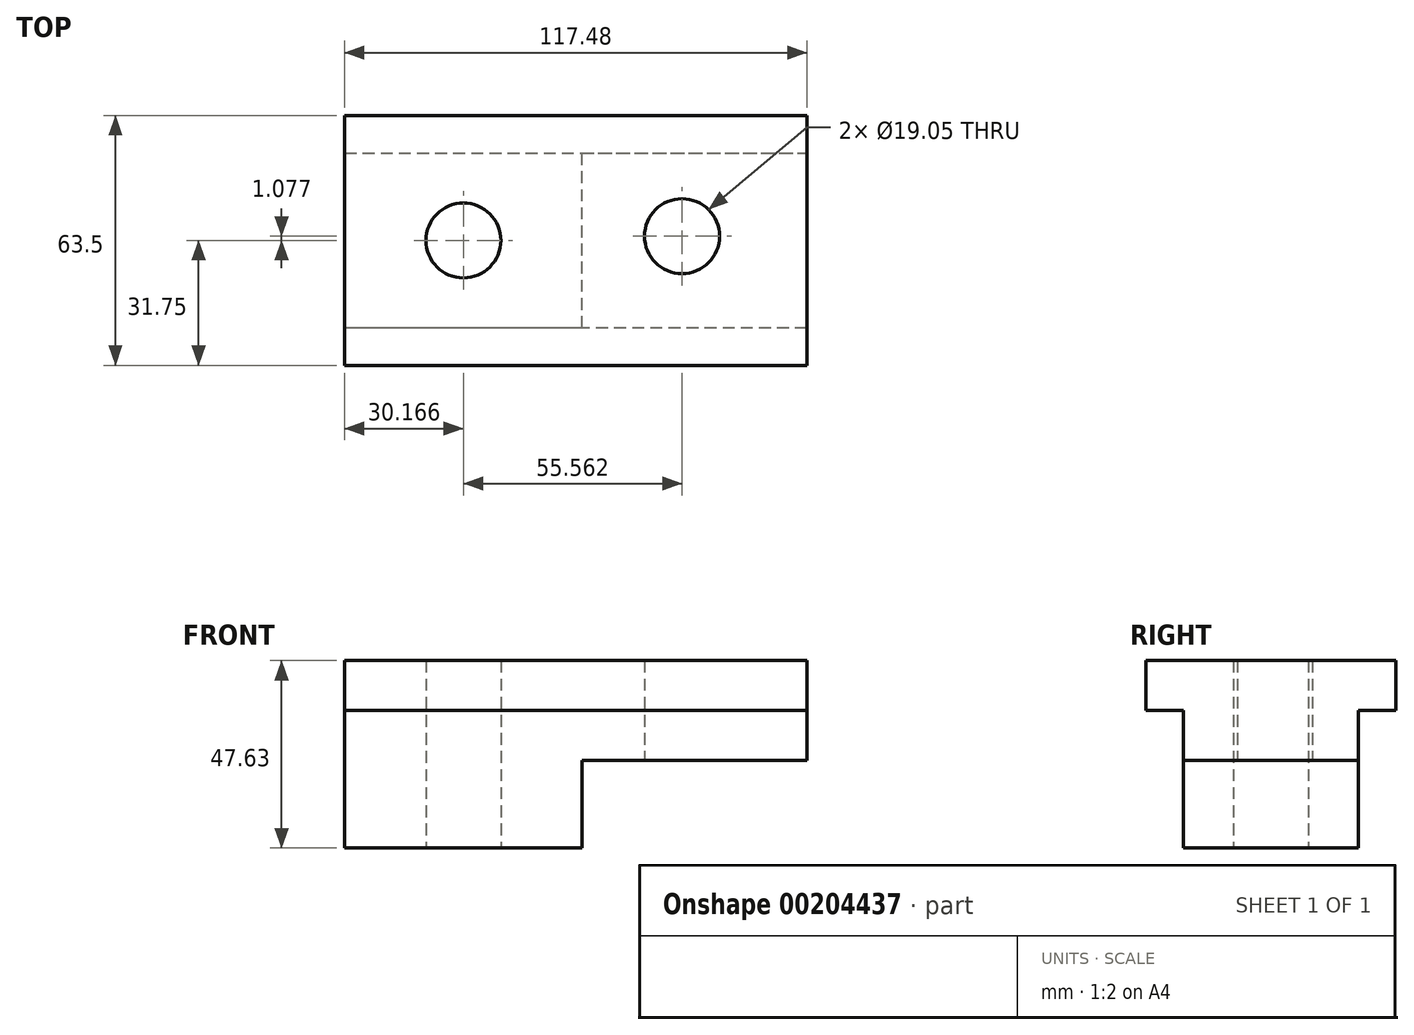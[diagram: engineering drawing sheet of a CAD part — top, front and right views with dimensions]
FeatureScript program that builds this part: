
annotation { "Feature Type Name" : "Feature", "Feature Type Description" : "" }
export const myFeature = defineFeature(function(context is Context, id is Id, definition is map)
    precondition{}
    {
        {
            var Q0;
            Q0=qCreatedBy(makeId("Top.planeOp"),FACE);
            var sketch = newSketch(context, id + "F0", { "sketchPlane" : qUnion([Q0])});
            skLineSegment(sketch, "E0.bottom", {"start": v(-57.42, 26.1) * mm, "end": v(60.06, 26.1) * mm});
            skLineSegment(sketch, "E0.top", {"start": v(-57.42, -37.4) * mm, "end": v(60.06, -37.4) * mm});
            skLineSegment(sketch, "E0.left", {"start": v(-57.42, 26.1) * mm, "end": v(-57.42, -37.4) * mm});
            skLineSegment(sketch, "E0.right", {"start": v(60.06, 26.1) * mm, "end": v(60.06, -37.4) * mm});
            skSolve(sketch);
        }
        {
            var Q0;
            Q0=makeQuery(id+"F0.imprint","IMPRINT",FACE,{"disambiguationData":[TD([[makeQuery(id+"F0.imprint","IMPRINT",EDGE,{"derivedFrom":sQuery(id+"F0.wireOp",EDGE,"E0.bottom")}),-1.0]])]});
            extrude(context, id + "F1", {"entities" : qUnion([Q0]), "depth" : 12.7 * mm});
        }
        {
            var Q0;
            Q0=makeQuery(id+"F1.opExtrude","CAP_FACE",FACE,{"disambiguationData":[OSD([sQuery(id+"F0.wireOp",EDGE,"E0.bottom"),sQuery(id+"F0.wireOp",EDGE,"E0.top"),sQuery(id+"F0.wireOp",EDGE,"E0.left"),sQuery(id+"F0.wireOp",EDGE,"E0.right")])],"isStart":true});
            var sketch = newSketch(context, id + "F2", { "sketchPlane" : qUnion([Q0])});
            skLineSegment(sketch, "E1", {"start": v(-57.42, -26.1) * mm, "end": v(-57.42, -16.57) * mm});
            skLineSegment(sketch, "E2", {"start": v(-57.42, 37.4) * mm, "end": v(-57.42, 27.88) * mm});
            skLineSegment(sketch, "E3", {"start": v(-57.42, -16.57) * mm, "end": v(60.06, -16.57) * mm});
            skLineSegment(sketch, "E4", {"start": v(60.06, -16.57) * mm, "end": v(60.06, 27.88) * mm});
            skLineSegment(sketch, "E5", {"start": v(60.06, 27.88) * mm, "end": v(-57.42, 27.88) * mm});
            skSolve(sketch);
        }
        {
            var Q0;
            {var subQ0=sQuery(id+"F2.wireOp",EDGE,"E3");Q0=makeQuery(id+"F2.imprint","IMPRINT",FACE,{"disambiguationData":[TD([[makeQuery(id+"F2.imprint","IMPRINT",EDGE,{"derivedFrom":subQ0}),1.0]])]});}
            extrude(context, id + "F3", {"entities" : qUnion([Q0]), "operationType" : NewBodyOperationType.ADD, "depth" : 12.7 * mm});
        }
        {
            var Q0;
            Q0=makeQuery(id+"F3.opExtrude","CAP_FACE",FACE,{"disambiguationData":[OSD([sQuery(id+"F0.wireOp",EDGE,"E0.left"),sQuery(id+"F2.wireOp",EDGE,"E3"),sQuery(id+"F2.wireOp",EDGE,"E4"),sQuery(id+"F2.wireOp",EDGE,"E5")])],"isStart":false});
            var sketch = newSketch(context, id + "F4", { "sketchPlane" : qUnion([Q0])});
            skLineSegment(sketch, "E6", {"start": v(-57.42, 27.88) * mm, "end": v(2.9, 27.88) * mm});
            skLineSegment(sketch, "E7", {"start": v(2.9, 27.88) * mm, "end": v(2.9, -16.57) * mm});
            skLineSegment(sketch, "E8", {"start": v(60.06, 27.88) * mm, "end": v(28.3, 27.88) * mm});
            skLineSegment(sketch, "E9", {"start": v(60.06, -16.57) * mm, "end": v(60.06, 4.57) * mm});
            skCircle(sketch, "E10", {"center": v(28.3, 4.57) * mm, "radius": 9.53 * mm});
            skSolve(sketch);
        }
        {
            var Q0;
            Q0=makeQuery(id+"F4.imprint","IMPRINT",FACE,{"disambiguationData":[TD([[makeQuery(id+"F4.imprint","IMPRINT",EDGE,{"derivedFrom":sQuery(id+"F4.wireOp",EDGE,"E6")}),1.0]])]});
            extrude(context, id + "F5", {"entities" : qUnion([Q0]), "operationType" : NewBodyOperationType.ADD, "depth" : 22.22 * mm});
        }
        {
            var Q0;
            Q0=makeQuery(id+"F4.imprint","IMPRINT",FACE,{"disambiguationData":[TD([[makeQuery(id+"F4.imprint","IMPRINT",EDGE,{"derivedFrom":sQuery(id+"F4.wireOp",EDGE,"E10")}),1.0]])]});
            extrude(context, id + "F6", {"entities" : qUnion([Q0]), "operationType" : NewBodyOperationType.REMOVE, "endBound" : BoundingType.THROUGH_ALL, "oppositeDirection" : true, "depth" : 25.4 * mm});
        }
        {
            var Q0;
            Q0=makeQuery(id+"F5.opExtrude","CAP_FACE",FACE,{"disambiguationData":[OSD([sQuery(id+"F0.wireOp",EDGE,"E0.left"),sQuery(id+"F2.wireOp",EDGE,"E3"),sQuery(id+"F4.wireOp",EDGE,"E6"),sQuery(id+"F4.wireOp",EDGE,"E7")])],"isStart":false});
            var sketch = newSketch(context, id + "F7", { "sketchPlane" : qUnion([Q0])});
            skLineSegment(sketch, "E11", {"start": v(-57.42, 27.88) * mm, "end": v(-27.25, 27.88) * mm});
            skLineSegment(sketch, "E12", {"start": v(-57.42, 27.88) * mm, "end": v(-57.42, 5.65) * mm});
            skCircle(sketch, "E13", {"center": v(-27.25, 5.65) * mm, "radius": 9.53 * mm});
            skSolve(sketch);
        }
        {
            var Q0;
            Q0=makeQuery(id+"F7.imprint","IMPRINT",FACE,{"disambiguationData":[TD([[makeQuery(id+"F7.imprint","IMPRINT",EDGE,{"derivedFrom":sQuery(id+"F7.wireOp",EDGE,"E13")}),1.0]])]});
            extrude(context, id + "F8", {"entities" : qUnion([Q0]), "operationType" : NewBodyOperationType.REMOVE, "endBound" : BoundingType.THROUGH_ALL, "oppositeDirection" : true, "depth" : 25.4 * mm});
        }
    });
